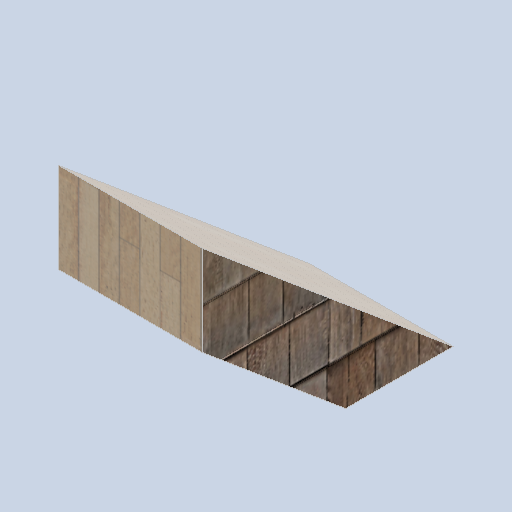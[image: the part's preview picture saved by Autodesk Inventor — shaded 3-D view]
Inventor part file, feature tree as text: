
AUTODESK INVENTOR PART (.ipt)
format: ipt  version: 2024.2 (Build 282272000, 272)  size: 169,472 bytes
history: native  units: in
note: dims shown in document units (in); Inventor stores cm internally (conversion verified against a paired STEP export)
features: other x3, sketch x1
ambient origin geometry x8: Origin, YZ Plane, XZ Plane, XY Plane, X Axis, Y Axis, Z Axis, Center Point
bodies: Body1 (feature_tree)
feature tree (4):
  other  "frame_rib_01_MIR.ipt"
  other  "Solid3::frame_rib_01_MIR.ipt"
  other  "TaggingFeature1"
  sketch  "Sketch1"  dims[d0=0.3937in]
